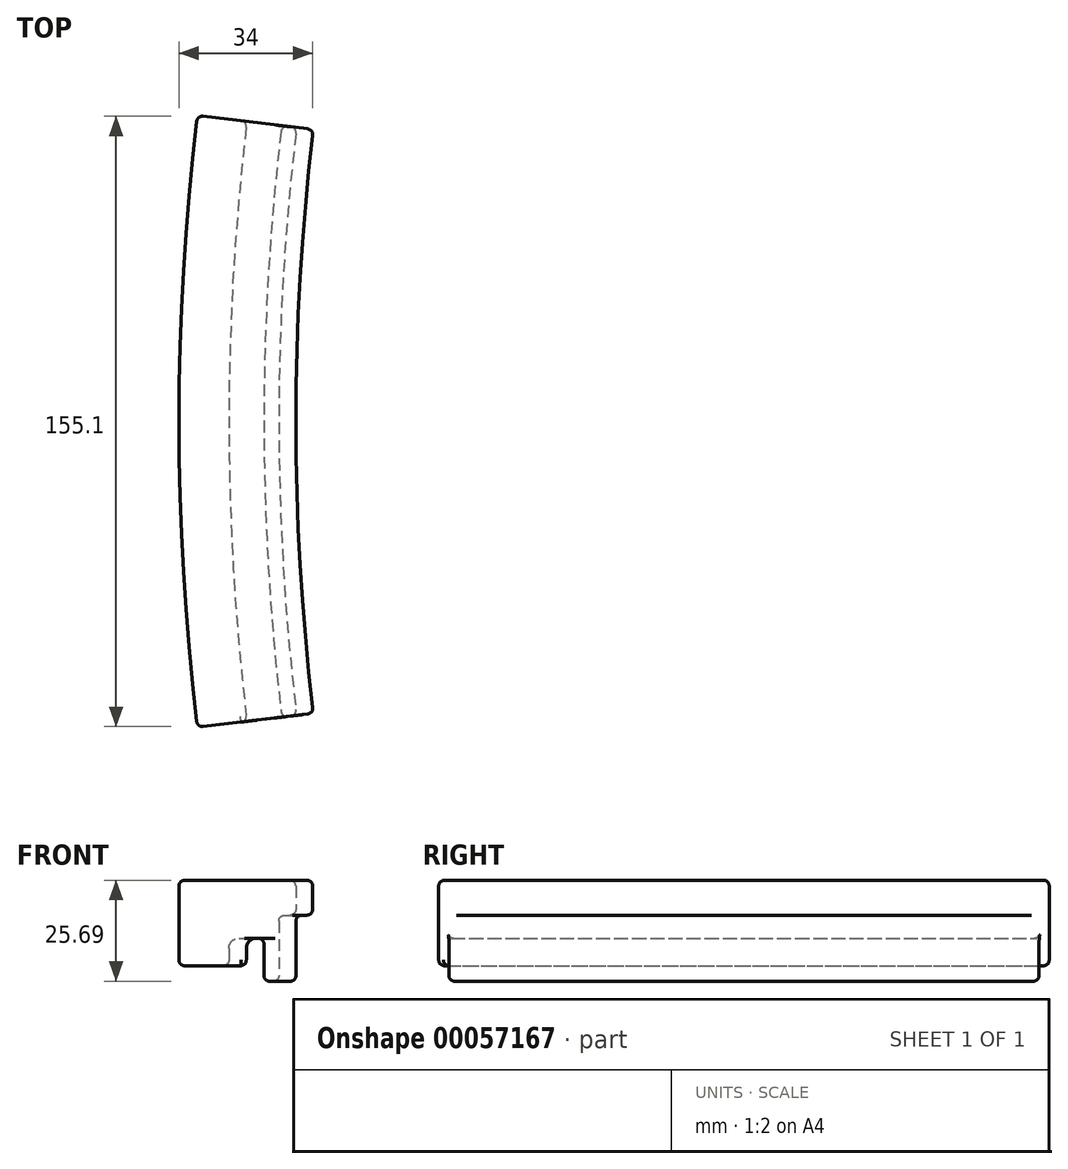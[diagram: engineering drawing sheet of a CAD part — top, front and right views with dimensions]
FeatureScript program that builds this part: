
annotation { "Feature Type Name" : "Feature", "Feature Type Description" : "" }
export const myFeature = defineFeature(function(context is Context, id is Id, definition is map)
    precondition{}
    {
        {
            var Q0;
            Q0=qCreatedBy(makeId("Front.planeOp"),FACE);
            var sketch = newSketch(context, id + "F0", { "sketchPlane" : qUnion([Q0])});
            skLineSegment(sketch, "E0", {"start": v(-20.75, -14.45) * mm, "end": v(-16.94, -14.45) * mm});
            skLineSegment(sketch, "E1", {"start": v(8.95, 7.3) * mm, "end": v(-20.75, 7.3) * mm});
            skLineSegment(sketch, "E2", {"start": v(-20.75, 7.3) * mm, "end": v(-20.75, -14.45) * mm});
            skLineSegment(sketch, "E3", {"start": v(-11.86, -14.45) * mm, "end": v(-8.05, -14.45) * mm});
            skLineSegment(sketch, "E4", {"start": v(-8.05, -14.45) * mm, "end": v(-8.05, -7.44) * mm});
            skLineSegment(sketch, "E5", {"start": v(-8.05, -7.44) * mm, "end": v(0.84, -7.44) * mm});
            skLineSegment(sketch, "E6", {"start": v(0.84, -7.44) * mm, "end": v(0.84, -18.38) * mm});
            skLineSegment(sketch, "E7", {"start": v(0.84, -18.38) * mm, "end": v(4.65, -18.38) * mm});
            skLineSegment(sketch, "E8", {"start": v(4.65, -18.38) * mm, "end": v(4.65, -1.58) * mm});
            skLineSegment(sketch, "E9", {"start": v(4.65, -1.58) * mm, "end": v(8.95, -1.58) * mm});
            skLineSegment(sketch, "E10", {"start": v(8.95, -1.58) * mm, "end": v(8.95, 7.3) * mm});
            skLineSegment(sketch, "E11", {"start": v(-16.94, -14.45) * mm, "end": v(-11.86, -14.45) * mm});
            skSolve(sketch);
        }
        {
            var Q0;
            Q0=qCreatedBy(makeId("Top.planeOp"),FACE);
            var sketch = newSketch(context, id + "F1", { "sketchPlane" : qUnion([Q0])});
            skLineSegment(sketch, "E12", {"start": v(0, 154.61) * mm, "end": v(0, -106.94) * mm, "construction": true});
            skLineSegment(sketch, "E13", {"start": v(-104.2, 0) * mm, "end": v(110.67, 0) * mm, "construction": true});
            skPoint(sketch, "E14.orphan", {"position": v(190.5, 0) * mm});
            skArc(sketch, "E15", {"start": v(-3.47, 76.2) * mm, "mid": v(-6.9, 38.17) * mm, "end": v(-8.05, 0) * mm});
            skLineSegment(sketch, "E16", {"start": v(-8.05, 0) * mm, "end": v(-8.05, -59.76) * mm, "construction": true});
            skSolve(sketch);
        }
        {
            var Q0;
            Q0=makeQuery(id+"F0.imprint","IMPRINT",FACE,{"disambiguationData":[TD([[makeQuery(id+"F0.imprint","IMPRINT",EDGE,{"derivedFrom":sQuery(id+"F0.wireOp",EDGE,"E0")}),1.0]])]});
            var Q1;
            Q1=sQuery(id+"F1.wireOp",EDGE,"E15");
            sweep(context, id + "F2", {"profiles" : qUnion([Q0]), "path" : qUnion([Q1])});
        }
        {
            var Q0;
            Q0=makeQuery(id+"F2.opSweep","SWEPT_BODY",BODY,{"disambiguationData":[OSD([sQuery(id+"F0.wireOp",EDGE,"E0"),sQuery(id+"F0.wireOp",EDGE,"E1"),sQuery(id+"F0.wireOp",EDGE,"E2"),sQuery(id+"F0.wireOp",EDGE,"BggQjnY6-MM8W-kzOd-og7T-KpAcLNo1pSnx"),sQuery(id+"F0.wireOp",EDGE,"xNtnLZgV-4XPD-CHvW-hVem-piVpDhwh1m0Q"),sQuery(id+"F0.wireOp",EDGE,"bckK7SNs-6UTo-fpJh-sIS0-AzvMCGTVYLUK"),sQuery(id+"F0.wireOp",EDGE,"E4"),sQuery(id+"F0.wireOp",EDGE,"E5"),sQuery(id+"F0.wireOp",EDGE,"E6"),sQuery(id+"F0.wireOp",EDGE,"E7"),sQuery(id+"F0.wireOp",EDGE,"E8"),sQuery(id+"F0.wireOp",EDGE,"E9"),sQuery(id+"F0.wireOp",EDGE,"E3"),sQuery(id+"F0.wireOp",EDGE,"E10"),sQuery(id+"F1.wireOp",EDGE,"E15")])]});
            var Q1;
            Q1=qCreatedBy(makeId("Front.planeOp"),FACE);
            mirror(context, id + "F3", {"operationType" : NewBodyOperationType.ADD, "entities" : qUnion([Q0]), "mirrorPlane" : qUnion([Q1])});
        }
        {
            var Q0;
            {var subQ0=makeQuery(id+"F2.opSweep","SWEPT_EDGE",EDGE,{"disambiguationData":[OSD([sQuery(id+"F0.wireOp",EDGE,"E4"),sQuery(id+"F0.wireOp",EDGE,"E5"),sQuery(id+"F1.wireOp",EDGE,"E15")])]});Q0=makeQuery(id+"F3.boolean.opBoolean","MERGE",EDGE,{"derivedFrom":[subQ0,makeQuery(id+"F3.opPattern","COPY",EDGE,{"derivedFrom":subQ0,"instanceName":"1"})]});}
            fillet(context, id + "F4", {"entities" : qUnion([Q0]), "radius" : 2.54 * mm, "tangentPropagation" : true, "allowEdgeOverflow" : false});
        }
        {
            var Q0;
            {var subQ0=makeQuery(id+"F2.opSweep","SWEPT_EDGE",EDGE,{"disambiguationData":[OSD([sQuery(id+"F0.wireOp",EDGE,"E5"),sQuery(id+"F0.wireOp",EDGE,"E6"),sQuery(id+"F1.wireOp",EDGE,"E15")])]});Q0=makeQuery(id+"F3.boolean.opBoolean","MERGE",EDGE,{"derivedFrom":[subQ0,makeQuery(id+"F3.opPattern","COPY",EDGE,{"derivedFrom":subQ0,"instanceName":"1"})]});}
            var Q1;
            {var subQ0=makeQuery(id+"F2.opSweep","SWEPT_EDGE",EDGE,{"disambiguationData":[OSD([sQuery(id+"F0.wireOp",EDGE,"E7"),sQuery(id+"F0.wireOp",EDGE,"E8"),sQuery(id+"F1.wireOp",EDGE,"E15")])]});Q1=makeQuery(id+"F3.boolean.opBoolean","MERGE",EDGE,{"derivedFrom":[subQ0,makeQuery(id+"F3.opPattern","COPY",EDGE,{"derivedFrom":subQ0,"instanceName":"1"})]});}
            var Q2;
            {var subQ0=makeQuery(id+"F2.opSweep","SWEPT_EDGE",EDGE,{"disambiguationData":[OSD([sQuery(id+"F0.wireOp",EDGE,"E6"),sQuery(id+"F0.wireOp",EDGE,"E7"),sQuery(id+"F1.wireOp",EDGE,"E15")])]});Q2=makeQuery(id+"F3.boolean.opBoolean","MERGE",EDGE,{"derivedFrom":[subQ0,makeQuery(id+"F3.opPattern","COPY",EDGE,{"derivedFrom":subQ0,"instanceName":"1"})]});}
            var Q3;
            {var subQ0=makeQuery(id+"F2.opSweep","SWEPT_EDGE",EDGE,{"disambiguationData":[OSD([sQuery(id+"F0.wireOp",EDGE,"E8"),sQuery(id+"F0.wireOp",EDGE,"E9"),sQuery(id+"F1.wireOp",EDGE,"E15")])]});Q3=makeQuery(id+"F3.boolean.opBoolean","MERGE",EDGE,{"derivedFrom":[subQ0,makeQuery(id+"F3.opPattern","COPY",EDGE,{"derivedFrom":subQ0,"instanceName":"1"})]});}
            var Q4;
            Q4=makeQuery(id+"F3.opPattern","COPY",EDGE,{"derivedFrom":makeQuery(id+"F2.opSweep","CAP_EDGE",EDGE,{"disambiguationData":[OSD([sQuery(id+"F0.wireOp",EDGE,"E7"),sQuery(id+"F1.wireOp",VERTEX,"E15.start")])],"isStart":false}),"instanceName":"1"});
            var Q5;
            Q5=makeQuery(id+"F2.opSweep","CAP_EDGE",EDGE,{"disambiguationData":[OSD([sQuery(id+"F0.wireOp",EDGE,"E7"),sQuery(id+"F1.wireOp",VERTEX,"E15.start")])],"isStart":false});
            var Q6;
            Q6=makeQuery(id+"F2.opSweep","CAP_EDGE",EDGE,{"disambiguationData":[OSD([sQuery(id+"F0.wireOp",EDGE,"E6"),sQuery(id+"F1.wireOp",VERTEX,"E15.start")])],"isStart":false});
            var Q7;
            Q7=makeQuery(id+"F3.opPattern","COPY",EDGE,{"derivedFrom":makeQuery(id+"F2.opSweep","CAP_EDGE",EDGE,{"disambiguationData":[OSD([sQuery(id+"F0.wireOp",EDGE,"E6"),sQuery(id+"F1.wireOp",VERTEX,"E15.start")])],"isStart":false}),"instanceName":"1"});
            var Q8;
            Q8=makeQuery(id+"F3.opPattern","COPY",EDGE,{"derivedFrom":makeQuery(id+"F2.opSweep","CAP_EDGE",EDGE,{"disambiguationData":[OSD([sQuery(id+"F0.wireOp",EDGE,"E8"),sQuery(id+"F1.wireOp",VERTEX,"E15.start")])],"isStart":false}),"instanceName":"1"});
            var Q9;
            {var subQ0=makeQuery(id+"F2.opSweep","SWEPT_EDGE",EDGE,{"disambiguationData":[OSD([sQuery(id+"F0.wireOp",EDGE,"E9"),sQuery(id+"F0.wireOp",EDGE,"E10"),sQuery(id+"F1.wireOp",EDGE,"E15")])]});Q9=makeQuery(id+"F3.boolean.opBoolean","MERGE",EDGE,{"derivedFrom":[subQ0,makeQuery(id+"F3.opPattern","COPY",EDGE,{"derivedFrom":subQ0,"instanceName":"1"})]});}
            var Q10;
            Q10=makeQuery(id+"F2.opSweep","CAP_EDGE",EDGE,{"disambiguationData":[OSD([sQuery(id+"F0.wireOp",EDGE,"E8"),sQuery(id+"F1.wireOp",VERTEX,"E15.start")])],"isStart":false});
            var Q11;
            Q11=makeQuery(id+"F3.opPattern","COPY",EDGE,{"derivedFrom":makeQuery(id+"F2.opSweep","CAP_EDGE",EDGE,{"disambiguationData":[OSD([sQuery(id+"F0.wireOp",EDGE,"E10"),sQuery(id+"F1.wireOp",VERTEX,"E15.start")])],"isStart":false}),"instanceName":"1"});
            var Q12;
            {var subQ0=makeQuery(id+"F2.opSweep","SWEPT_EDGE",EDGE,{"disambiguationData":[OSD([sQuery(id+"F0.wireOp",EDGE,"E1"),sQuery(id+"F0.wireOp",EDGE,"E10"),sQuery(id+"F1.wireOp",EDGE,"E15")])]});Q12=makeQuery(id+"F3.boolean.opBoolean","MERGE",EDGE,{"derivedFrom":[subQ0,makeQuery(id+"F3.opPattern","COPY",EDGE,{"derivedFrom":subQ0,"instanceName":"1"})]});}
            var Q13;
            Q13=makeQuery(id+"F3.opPattern","COPY",EDGE,{"derivedFrom":makeQuery(id+"F2.opSweep","CAP_EDGE",EDGE,{"disambiguationData":[OSD([sQuery(id+"F0.wireOp",EDGE,"E1"),sQuery(id+"F1.wireOp",VERTEX,"E15.start")])],"isStart":false}),"instanceName":"1"});
            var Q14;
            Q14=makeQuery(id+"F3.opPattern","COPY",EDGE,{"derivedFrom":makeQuery(id+"F2.opSweep","CAP_EDGE",EDGE,{"disambiguationData":[OSD([sQuery(id+"F0.wireOp",EDGE,"E2"),sQuery(id+"F1.wireOp",VERTEX,"E15.start")])],"isStart":false}),"instanceName":"1"});
            var Q15;
            {var subQ0=makeQuery(id+"F2.opSweep","SWEPT_EDGE",EDGE,{"disambiguationData":[OSD([sQuery(id+"F0.wireOp",EDGE,"E1"),sQuery(id+"F0.wireOp",EDGE,"E2"),sQuery(id+"F1.wireOp",EDGE,"E15")])]});Q15=makeQuery(id+"F3.boolean.opBoolean","MERGE",EDGE,{"derivedFrom":[subQ0,makeQuery(id+"F3.opPattern","COPY",EDGE,{"derivedFrom":subQ0,"instanceName":"1"})]});}
            var Q16;
            Q16=makeQuery(id+"F3.opPattern","COPY",EDGE,{"derivedFrom":makeQuery(id+"F2.opSweep","CAP_EDGE",EDGE,{"disambiguationData":[OSD([sQuery(id+"F0.wireOp",EDGE,"xNtnLZgV-4XPD-CHvW-hVem-piVpDhwh1m0Q"),sQuery(id+"F1.wireOp",VERTEX,"E15.start")])],"isStart":false}),"instanceName":"1"});
            var Q17;
            Q17=makeQuery(id+"F3.opPattern","COPY",EDGE,{"derivedFrom":makeQuery(id+"F2.opSweep","CAP_EDGE",EDGE,{"disambiguationData":[OSD([sQuery(id+"F0.wireOp",EDGE,"E3"),sQuery(id+"F1.wireOp",VERTEX,"E15.start")])],"isStart":false}),"instanceName":"1"});
            var Q18;
            Q18=makeQuery(id+"F3.opPattern","COPY",EDGE,{"derivedFrom":makeQuery(id+"F2.opSweep","CAP_EDGE",EDGE,{"disambiguationData":[OSD([sQuery(id+"F0.wireOp",EDGE,"bckK7SNs-6UTo-fpJh-sIS0-AzvMCGTVYLUK"),sQuery(id+"F1.wireOp",VERTEX,"E15.start")])],"isStart":false}),"instanceName":"1"});
            var Q19;
            Q19=makeQuery(id+"F3.opPattern","COPY",EDGE,{"derivedFrom":makeQuery(id+"F2.opSweep","CAP_EDGE",EDGE,{"disambiguationData":[OSD([sQuery(id+"F0.wireOp",EDGE,"BggQjnY6-MM8W-kzOd-og7T-KpAcLNo1pSnx"),sQuery(id+"F1.wireOp",VERTEX,"E15.start")])],"isStart":false}),"instanceName":"1"});
            var Q20;
            Q20=makeQuery(id+"F3.opPattern","COPY",EDGE,{"derivedFrom":makeQuery(id+"F2.opSweep","CAP_EDGE",EDGE,{"disambiguationData":[OSD([sQuery(id+"F0.wireOp",EDGE,"E0"),sQuery(id+"F1.wireOp",VERTEX,"E15.start")])],"isStart":false}),"instanceName":"1"});
            var Q21;
            {var subQ0=makeQuery(id+"F2.opSweep","SWEPT_EDGE",EDGE,{"disambiguationData":[OSD([sQuery(id+"F0.wireOp",EDGE,"BggQjnY6-MM8W-kzOd-og7T-KpAcLNo1pSnx"),sQuery(id+"F0.wireOp",EDGE,"xNtnLZgV-4XPD-CHvW-hVem-piVpDhwh1m0Q"),sQuery(id+"F1.wireOp",EDGE,"E15")])]});Q21=makeQuery(id+"F3.boolean.opBoolean","MERGE",EDGE,{"derivedFrom":[subQ0,makeQuery(id+"F3.opPattern","COPY",EDGE,{"derivedFrom":subQ0,"instanceName":"1"})]});}
            var Q22;
            {var subQ0=makeQuery(id+"F2.opSweep","SWEPT_EDGE",EDGE,{"disambiguationData":[OSD([sQuery(id+"F0.wireOp",EDGE,"xNtnLZgV-4XPD-CHvW-hVem-piVpDhwh1m0Q"),sQuery(id+"F0.wireOp",EDGE,"bckK7SNs-6UTo-fpJh-sIS0-AzvMCGTVYLUK"),sQuery(id+"F1.wireOp",EDGE,"E15")])]});Q22=makeQuery(id+"F3.boolean.opBoolean","MERGE",EDGE,{"derivedFrom":[subQ0,makeQuery(id+"F3.opPattern","COPY",EDGE,{"derivedFrom":subQ0,"instanceName":"1"})]});}
            var Q23;
            {var subQ0=makeQuery(id+"F2.opSweep","SWEPT_EDGE",EDGE,{"disambiguationData":[OSD([sQuery(id+"F0.wireOp",EDGE,"bckK7SNs-6UTo-fpJh-sIS0-AzvMCGTVYLUK"),sQuery(id+"F0.wireOp",EDGE,"E3"),sQuery(id+"F1.wireOp",EDGE,"E15")])]});Q23=makeQuery(id+"F3.boolean.opBoolean","MERGE",EDGE,{"derivedFrom":[subQ0,makeQuery(id+"F3.opPattern","COPY",EDGE,{"derivedFrom":subQ0,"instanceName":"1"})]});}
            var Q24;
            {var subQ0=makeQuery(id+"F2.opSweep","SWEPT_EDGE",EDGE,{"disambiguationData":[OSD([sQuery(id+"F0.wireOp",EDGE,"E4"),sQuery(id+"F0.wireOp",EDGE,"E3"),sQuery(id+"F1.wireOp",EDGE,"E15")])]});Q24=makeQuery(id+"F3.boolean.opBoolean","MERGE",EDGE,{"derivedFrom":[subQ0,makeQuery(id+"F3.opPattern","COPY",EDGE,{"derivedFrom":subQ0,"instanceName":"1"})]});}
            var Q25;
            {var subQ0=makeQuery(id+"F2.opSweep","SWEPT_EDGE",EDGE,{"disambiguationData":[OSD([sQuery(id+"F0.wireOp",EDGE,"E0"),sQuery(id+"F0.wireOp",EDGE,"BggQjnY6-MM8W-kzOd-og7T-KpAcLNo1pSnx"),sQuery(id+"F1.wireOp",EDGE,"E15")])]});Q25=makeQuery(id+"F3.boolean.opBoolean","MERGE",EDGE,{"derivedFrom":[subQ0,makeQuery(id+"F3.opPattern","COPY",EDGE,{"derivedFrom":subQ0,"instanceName":"1"})]});}
            var Q26;
            {var subQ0=makeQuery(id+"F2.opSweep","SWEPT_EDGE",EDGE,{"disambiguationData":[OSD([sQuery(id+"F0.wireOp",EDGE,"E0"),sQuery(id+"F0.wireOp",EDGE,"E2"),sQuery(id+"F1.wireOp",EDGE,"E15")])]});Q26=makeQuery(id+"F3.boolean.opBoolean","MERGE",EDGE,{"derivedFrom":[subQ0,makeQuery(id+"F3.opPattern","COPY",EDGE,{"derivedFrom":subQ0,"instanceName":"1"})]});}
            var Q27;
            Q27=makeQuery(id+"F2.opSweep","CAP_EDGE",EDGE,{"disambiguationData":[OSD([sQuery(id+"F0.wireOp",EDGE,"E0"),sQuery(id+"F1.wireOp",VERTEX,"E15.start")])],"isStart":false});
            var Q28;
            Q28=makeQuery(id+"F2.opSweep","CAP_EDGE",EDGE,{"disambiguationData":[OSD([sQuery(id+"F0.wireOp",EDGE,"E2"),sQuery(id+"F1.wireOp",VERTEX,"E15.start")])],"isStart":false});
            var Q29;
            Q29=makeQuery(id+"F2.opSweep","CAP_EDGE",EDGE,{"disambiguationData":[OSD([sQuery(id+"F0.wireOp",EDGE,"E3"),sQuery(id+"F1.wireOp",VERTEX,"E15.start")])],"isStart":false});
            var Q30;
            Q30=makeQuery(id+"F2.opSweep","CAP_EDGE",EDGE,{"disambiguationData":[OSD([sQuery(id+"F0.wireOp",EDGE,"xNtnLZgV-4XPD-CHvW-hVem-piVpDhwh1m0Q"),sQuery(id+"F1.wireOp",VERTEX,"E15.start")])],"isStart":false});
            var Q31;
            Q31=makeQuery(id+"F2.opSweep","CAP_EDGE",EDGE,{"disambiguationData":[OSD([sQuery(id+"F0.wireOp",EDGE,"E1"),sQuery(id+"F1.wireOp",VERTEX,"E15.start")])],"isStart":false});
            var Q32;
            Q32=makeQuery(id+"F2.opSweep","CAP_EDGE",EDGE,{"disambiguationData":[OSD([sQuery(id+"F0.wireOp",EDGE,"E10"),sQuery(id+"F1.wireOp",VERTEX,"E15.start")])],"isStart":false});
            fillet(context, id + "F5", {"entities" : qUnion([Q0, Q1, Q2, Q3, Q4, Q5, Q6, Q7, Q8, Q9, Q10, Q11, Q12, Q13, Q14, Q15, Q16, Q17, Q18, Q19, Q20, Q21, Q22, Q23, Q24, Q25, Q26, Q27, Q28, Q29, Q30, Q31, Q32]), "radius" : 1.5 * mm, "tangentPropagation" : true, "allowEdgeOverflow" : false});
        }
    });
